# Revit family: Desk-Low_Secondary-Teknion-B_MPG-Run-Off_WS_with_End_Support-R2015
name_source: partatom
category: Furniture
revit_build: Autodesk Revit Architecture 2015 (Build: 20140323_1530(x64)
units: mm (PartAtom-declared; Revit-internal decimal feet)

## types (3) — shared parameters
Assembly Code = E2020200
Height = 28.811 "
Manufacturer = Teknion
Manufacturer Fax = 416.661.4586
Part Number = B_MPG
Product Documentation Link = http://www.teknion.com
Product Line = Expansion Casegoods
Product Page URL = http://www.teknion.com
Series = Expansion Casegoods
Sustainability Data = http://www.teknion.com
URL = www.teknion.com
Unit Weight URL = http://www.teknion.com
Warranty = http://www.teknion.com

## per-type parameters (varying)
| type | Description | Model | Thickness |
| 1-3/16" Thick | Run-Off Worksurface with End Support – Low Secondary Desk, 1-3/16" Thick | BMMPGQ__CNN | 1.189 " |
| 1" Thick | Run-Off Worksurface with End Support – Low Secondary Desk, 1" Thick | BDMPGQ__CNN | 1.026 " |
| 1-9/16" Thick | Run-Off Worksurface with End Support – Low Secondary Desk, 1-9/16" Thick | BXMPGQ__CNN | 1.555 " |

## geometry (parser evidence)
native form markers: Sweep x2
no freeform markers — native parametric forms only
